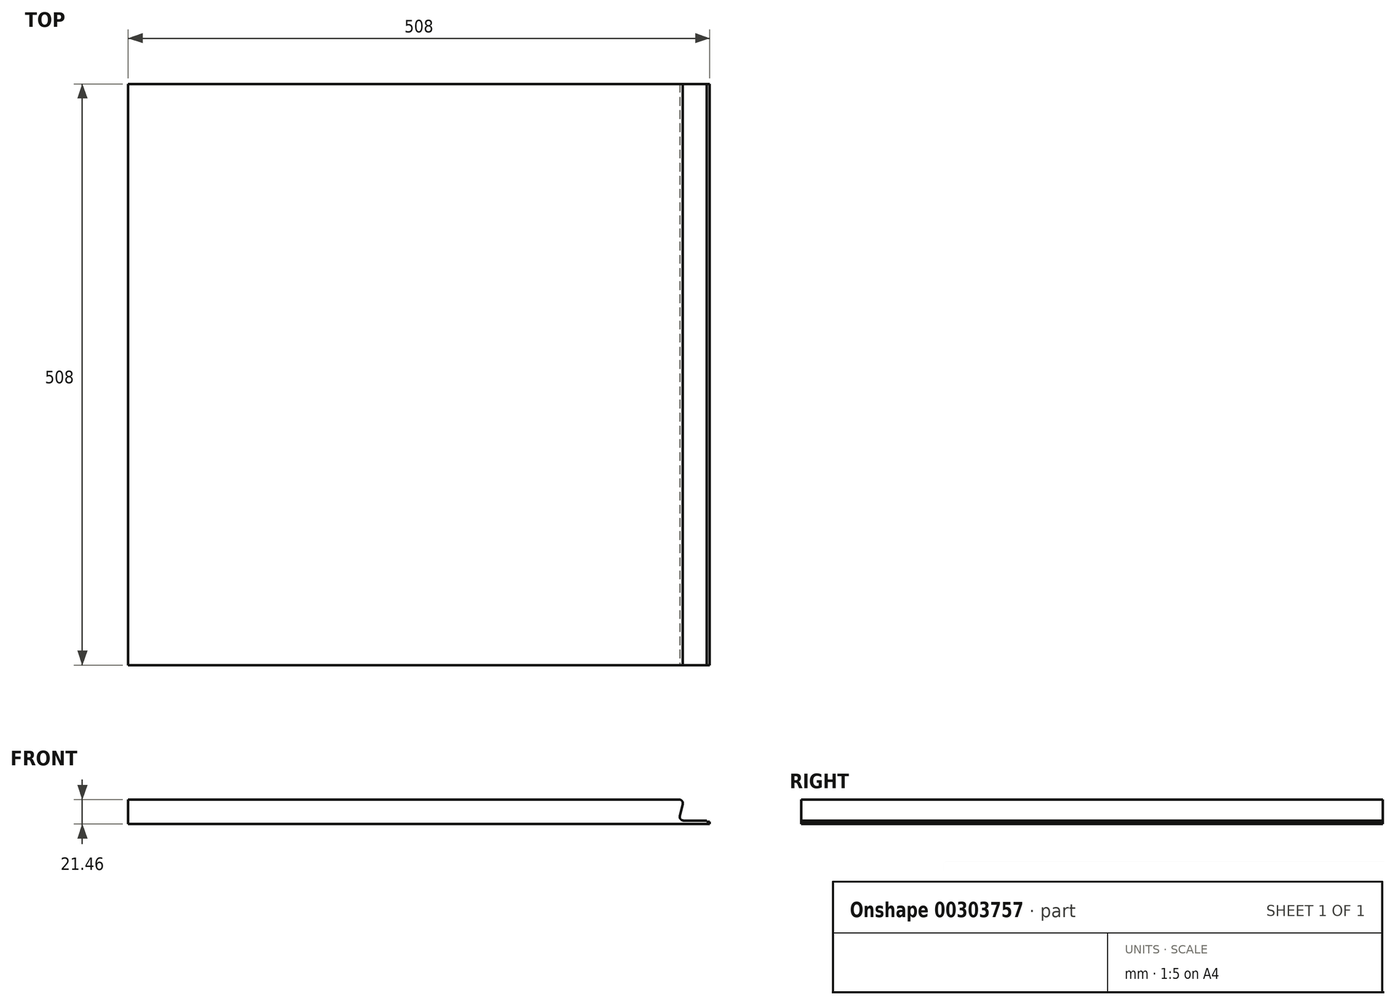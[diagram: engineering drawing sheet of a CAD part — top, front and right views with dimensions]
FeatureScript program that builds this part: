
annotation { "Feature Type Name" : "Feature", "Feature Type Description" : "" }
export const myFeature = defineFeature(function(context is Context, id is Id, definition is map)
    precondition{}
    {
        {
            var Q0;
            Q0=qCreatedBy(makeId("Front.planeOp"),FACE);
            var sketch = newSketch(context, id + "F0", { "sketchPlane" : qUnion([Q0])});
            skLineSegment(sketch, "E0", {"start": v(0, 0) * mm, "end": v(0, 1.9) * mm});
            skLineSegment(sketch, "E1", {"start": v(0, 1.9) * mm, "end": v(-2.54, 1.9) * mm});
            skLineSegment(sketch, "E2", {"start": v(-2.54, 1.9) * mm, "end": v(-2.54, 3.1) * mm});
            skLineSegment(sketch, "E3", {"start": v(-2.54, 3.1) * mm, "end": v(-22.91, 3.1) * mm});
            skLineSegment(sketch, "E4", {"start": v(-26.11, 7.2) * mm, "end": v(-23.58, 17.36) * mm});
            skLineSegment(sketch, "E5", {"start": v(-26.78, 21.46) * mm, "end": v(-508, 21.46) * mm});
            skLineSegment(sketch, "E6", {"start": v(-508, 21.46) * mm, "end": v(-508, 0) * mm});
            skLineSegment(sketch, "E7", {"start": v(-508, 0) * mm, "end": v(0, 0) * mm});
            skPoint(sketch, "E8.visualSharp", {"position": v(-27.14, 3.1) * mm});
            skArc(sketch, "E8.filletArc", {"start": v(-26.11, 7.2) * mm, "mid": v(-25.51, 4.37) * mm, "end": v(-22.91, 3.1) * mm});
            skPoint(sketch, "E9.visualSharp", {"position": v(-22.56, 21.46) * mm});
            skArc(sketch, "E9.filletArc", {"start": v(-23.58, 17.36) * mm, "mid": v(-24.18, 20.2) * mm, "end": v(-26.78, 21.46) * mm});
            skSolve(sketch);
        }
        {
            var Q0;
            Q0=makeQuery(id+"F0.imprint","IMPRINT",FACE,{"disambiguationData":[TD([[makeQuery(id+"F0.imprint","IMPRINT",EDGE,{"derivedFrom":sQuery(id+"F0.wireOp",EDGE,"E0")}),1.0]])]});
            extrude(context, id + "F1", {"entities" : qUnion([Q0]), "oppositeDirection" : true, "depth" : 508 * mm});
        }
    });
